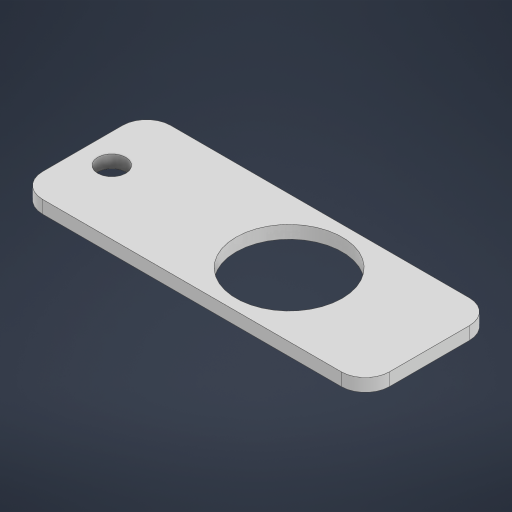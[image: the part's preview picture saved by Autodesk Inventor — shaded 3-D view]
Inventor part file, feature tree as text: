
AUTODESK INVENTOR PART (.ipt)
format: ipt  version: 2023 (Build 270158000, 158)  size: 194,560 bytes
history: native  units: in
note: dims shown in document units (in); Inventor stores cm internally (conversion verified against a paired STEP export)
features: extrude x1, sketch x1
ambient origin geometry x8: Origin, YZ Plane, XZ Plane, XY Plane, X Axis, Y Axis, Z Axis, Center Point
bodies: Solid1 (feature_tree)
feature tree (2):
  extrude  "Extrusion1"  Depth=0.6299in
  sketch  "Sketch1"  dims[d0=0.5217in d1=0.6299in d6=0.063in d7=0.0in d9=0.1181in d16=0.0049in d20=0.315in d22=1.0157in d24=0.4291in d25=0.1378in d26=0.1437in]
